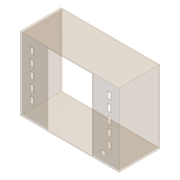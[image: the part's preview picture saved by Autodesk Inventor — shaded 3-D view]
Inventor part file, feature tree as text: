
AUTODESK INVENTOR PART (.ipt)
format: ipt  version: 2012 (Build 160160000, 160)  size: 152,576 bytes
history: native  units: in
note: dims shown in document units (in); Inventor stores cm internally (conversion verified against a paired STEP export)
features: extrude x5, sketch x5, pattern_linear x1
ambient origin geometry x8: Origin, YZ Plane, XZ Plane, XY Plane, X Axis, Y Axis, Z Axis, Center Point
bodies: Solid1 (feature_tree)
feature tree (11):
  extrude  "Extrusion1"  Depth=0.25in
  extrude  "Extrusion2"  Depth=0.25in
  extrude  "Extrusion3"  Depth=17.0in
  extrude  "Extrusion4"  Depth=0.25in
  pattern_linear  "Rectangular Pattern1"  Spacing1=0.25in  [1 undecoded]
  extrude  "Extrusion5"  Depth=6.0in TaperAngle=0.0deg
  sketch  "Sketch1"  dims[d0=0.25in d1=0.25in]
  sketch  "Sketch2"  dims[d2=0.25in d3=0.25in]
  sketch  "Sketch3"  dims[d4=23.0in d5=17.0in]
  sketch  "Sketch4"  dims[d6=9.5in d7=0.0in d8=0.25in]
  sketch  "Sketch5"  dims[d9=6.0in d10=0.0in d11=0.25in d12=6.0in d13=0.0in d14=0.75in d15=1.5in d16=4.0in d17=0.0in d18=1.9685in d20=2.5in d21=0.7874in d23=18.0in d24=1.0in d25=2.5in d26=2.0in d27=4.0in d28=0.0in d29=2.25in d30=2.0in]
note: 1 required parameter value undecoded (feature->parameter linkage not recoverable at this tier; creation-order binding heuristic only, values carry confidence <= 0.55)
